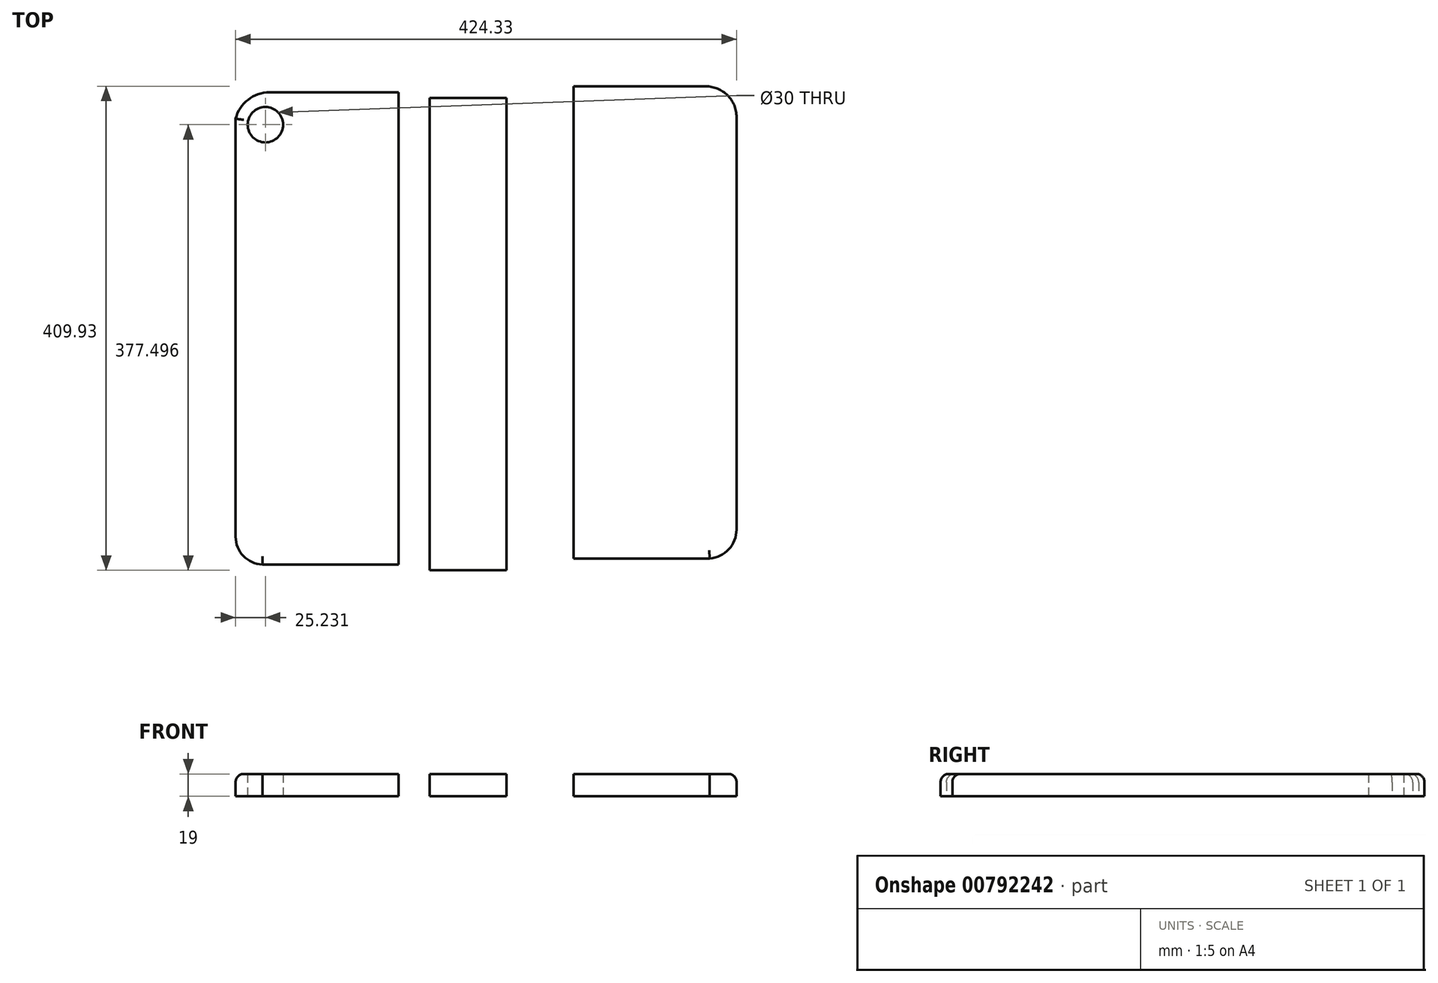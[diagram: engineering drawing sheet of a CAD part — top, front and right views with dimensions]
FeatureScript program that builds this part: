
annotation { "Feature Type Name" : "Feature", "Feature Type Description" : "" }
export const myFeature = defineFeature(function(context is Context, id is Id, definition is map)
    precondition{}
    {
        {
            var Q0;
            Q0=qCreatedBy(makeId("Top.planeOp"),FACE);
            var sketch = newSketch(context, id + "F0", { "sketchPlane" : qUnion([Q0])});
            skLineSegment(sketch, "E0.bottom", {"start": v(-87.35, -156.8) * mm, "end": v(-202.6, -156.8) * mm});
            skLineSegment(sketch, "E0.top", {"start": v(-87.35, 243.2) * mm, "end": v(-196.45, 243.2) * mm});
            skLineSegment(sketch, "E0.left", {"start": v(-87.35, -156.8) * mm, "end": v(-87.35, 243.2) * mm});
            skLineSegment(sketch, "E1.bottom", {"start": v(-60.98, -161.74) * mm, "end": v(4.02, -161.74) * mm});
            skLineSegment(sketch, "E1.top", {"start": v(-60.98, 238.26) * mm, "end": v(4.02, 238.26) * mm});
            skLineSegment(sketch, "E1.left", {"start": v(-60.98, -161.74) * mm, "end": v(-60.98, 238.26) * mm});
            skLineSegment(sketch, "E1.right", {"start": v(4.02, -161.74) * mm, "end": v(4.02, 238.26) * mm});
            skLineSegment(sketch, "E2.bottom", {"start": v(60.98, -151.81) * mm, "end": v(176.2, -151.81) * mm});
            skLineSegment(sketch, "E2.top", {"start": v(60.98, 248.19) * mm, "end": v(173.11, 248.19) * mm});
            skLineSegment(sketch, "E2.left", {"start": v(60.98, -151.81) * mm, "end": v(60.98, 248.19) * mm});
            skPoint(sketch, "E3", {"position": v(-200.12, 215.76) * mm});
            skLineSegment(sketch, "E4", {"start": v(-225.35, -133.39) * mm, "end": v(-225.35, 220.77) * mm});
            skArc(sketch, "E5", {"start": v(-225.35, -133.39) * mm, "mid": v(-218.73, -149.7) * mm, "end": v(-202.6, -156.8) * mm});
            skLineSegment(sketch, "E6", {"start": v(198.98, -127.23) * mm, "end": v(198.98, 222.31) * mm});
            skArc(sketch, "E7", {"start": v(-196.45, 243.2) * mm, "mid": v(-214.74, 236.93) * mm, "end": v(-225.35, 220.77) * mm});
            skArc(sketch, "E8", {"start": v(173.11, 248.19) * mm, "mid": v(191.4, 240.61) * mm, "end": v(198.98, 222.31) * mm});
            skArc(sketch, "E9", {"start": v(198.98, -127.23) * mm, "mid": v(192.4, -143.99) * mm, "end": v(176.2, -151.81) * mm});
            skSolve(sketch);
        }
        {
            var Q0;
            Q0=makeQuery(id+"F0.imprint","IMPRINT",FACE,{"disambiguationData":[TD([[makeQuery(id+"F0.imprint","IMPRINT",EDGE,{"derivedFrom":sQuery(id+"F0.wireOp",EDGE,"E0.bottom")}),-1.0]])]});
            var Q1;
            Q1=makeQuery(id+"F0.imprint","IMPRINT",FACE,{"disambiguationData":[TD([[makeQuery(id+"F0.imprint","IMPRINT",EDGE,{"derivedFrom":sQuery(id+"F0.wireOp",EDGE,"E1.bottom")}),1.0]])]});
            var Q2;
            Q2=makeQuery(id+"F0.imprint","IMPRINT",FACE,{"disambiguationData":[TD([[makeQuery(id+"F0.imprint","IMPRINT",EDGE,{"derivedFrom":sQuery(id+"F0.wireOp",EDGE,"E2.bottom")}),1.0]])]});
            extrude(context, id + "F1", {"entities" : qUnion([Q0, Q1, Q2]), "depth" : 19 * mm, "offsetDistance" : 25 * mm});
        }
        {
            var Q0;
            Q0=makeQuery(id+"F1.opExtrude","CAP_EDGE",EDGE,{"disambiguationData":[OSD([sQuery(id+"F0.wireOp",EDGE,"E4")])],"isStart":false});
            var Q1;
            Q1=makeQuery(id+"F1.opExtrude","CAP_EDGE",EDGE,{"disambiguationData":[OSD([sQuery(id+"F0.wireOp",EDGE,"E0.bottom")])],"isStart":false});
            var Q2;
            Q2=makeQuery(id+"F1.opExtrude","CAP_EDGE",EDGE,{"disambiguationData":[OSD([sQuery(id+"F0.wireOp",EDGE,"E5")])],"isStart":false});
            var Q3;
            Q3=makeQuery(id+"F1.opExtrude","CAP_EDGE",EDGE,{"disambiguationData":[OSD([sQuery(id+"F0.wireOp",EDGE,"E7")])],"isStart":false});
            var Q4;
            Q4=makeQuery(id+"F1.opExtrude","CAP_EDGE",EDGE,{"disambiguationData":[OSD([sQuery(id+"F0.wireOp",EDGE,"E0.top")])],"isStart":false});
            var Q5;
            Q5=makeQuery(id+"F1.opExtrude","CAP_EDGE",EDGE,{"disambiguationData":[OSD([sQuery(id+"F0.wireOp",EDGE,"E2.top")])],"isStart":false});
            var Q6;
            Q6=makeQuery(id+"F1.opExtrude","CAP_EDGE",EDGE,{"disambiguationData":[OSD([sQuery(id+"F0.wireOp",EDGE,"E8")])],"isStart":false});
            var Q7;
            Q7=makeQuery(id+"F1.opExtrude","CAP_EDGE",EDGE,{"disambiguationData":[OSD([sQuery(id+"F0.wireOp",EDGE,"E6")])],"isStart":false});
            var Q8;
            Q8=makeQuery(id+"F1.opExtrude","CAP_EDGE",EDGE,{"disambiguationData":[OSD([sQuery(id+"F0.wireOp",EDGE,"E9")])],"isStart":false});
            var Q9;
            Q9=makeQuery(id+"F1.opExtrude","CAP_EDGE",EDGE,{"disambiguationData":[OSD([sQuery(id+"F0.wireOp",EDGE,"E2.bottom")])],"isStart":false});
            var Q10;
            Q10=makeQuery(id+"F1.opExtrude","CAP_EDGE",EDGE,{"disambiguationData":[OSD([sQuery(id+"F0.wireOp",EDGE,"E1.top")])],"isStart":false});
            var Q11;
            Q11=makeQuery(id+"F1.opExtrude","CAP_EDGE",EDGE,{"disambiguationData":[OSD([sQuery(id+"F0.wireOp",EDGE,"E1.bottom")])],"isStart":false});
            fillet(context, id + "F2", {"entities" : qUnion([Q0, Q1, Q2, Q3, Q4, Q5, Q6, Q7, Q8, Q9, Q10, Q11]), "radius" : 7 * mm, "tangentPropagation" : true, "allowEdgeOverflow" : false});
        }
        {
            var Q0;
            Q0=sQuery(id+"F0.wireOp",VERTEX,"E3");
            var Q1;
            Q1=makeQuery(id+"F1.opExtrude","SWEPT_BODY",BODY,{"disambiguationData":[OSD([sQuery(id+"F0.wireOp",EDGE,"E0.bottom"),sQuery(id+"F0.wireOp",EDGE,"E0.top"),sQuery(id+"F0.wireOp",EDGE,"E0.left"),sQuery(id+"F0.wireOp",EDGE,"E0.right")])]});
            hole(context, id + "F3", {"style" : HoleStyle.SIMPLE, "endStyle" : HoleEndStyle.THROUGH, "oppositeDirection" : true, "holeDiameter" : 30 * mm, "majorDiameter" : 5 * mm, "isTappedThrough" : true, "tappedDepth" : 12 * mm, "tapClearance" : 3, "locations" : qUnion([Q0]), "scope" : qUnion([Q1])});
        }
    });
